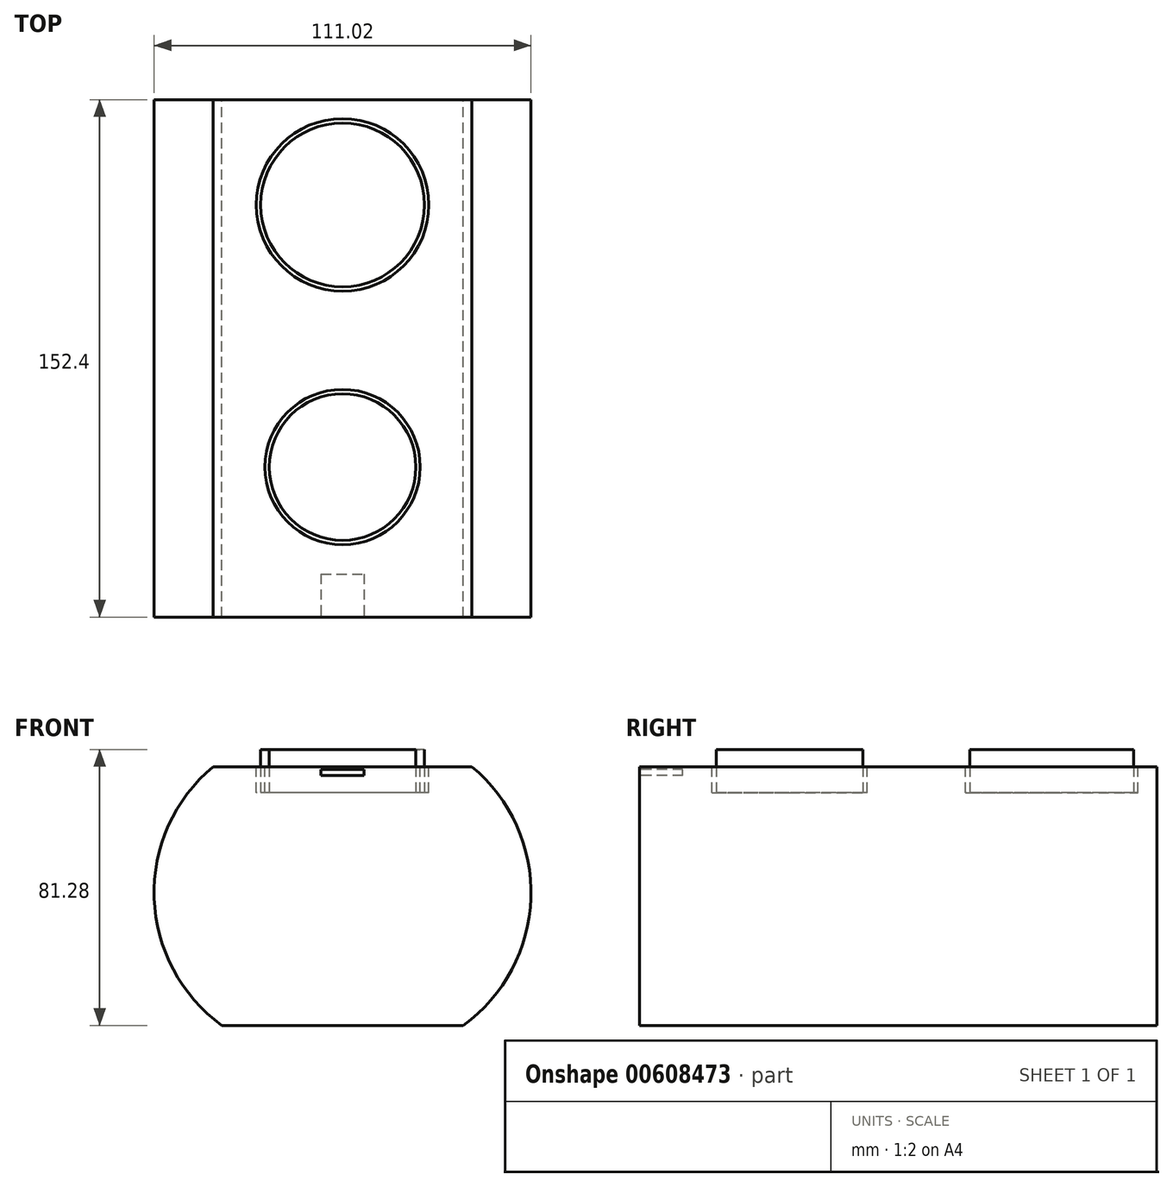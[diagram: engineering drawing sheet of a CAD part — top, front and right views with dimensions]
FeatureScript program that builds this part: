
annotation { "Feature Type Name" : "Feature", "Feature Type Description" : "" }
export const myFeature = defineFeature(function(context is Context, id is Id, definition is map)
    precondition{}
    {
        {
            var Q0;
            Q0=qCreatedBy(makeId("Front.planeOp"),FACE);
            var sketch = newSketch(context, id + "F0", { "sketchPlane" : qUnion([Q0])});
            skLineSegment(sketch, "E0", {"start": v(0, 0) * mm, "end": v(0, 76.2) * mm});
            skLineSegment(sketch, "E1", {"start": v(0, 76.2) * mm, "end": v(-38.1, 76.2) * mm});
            skLineSegment(sketch, "E2", {"start": v(0, 0) * mm, "end": v(-35.56, 0) * mm});
            skArc(sketch, "E3", {"start": v(-38.1, 76.2) * mm, "mid": v(-55.49, 37.48) * mm, "end": v(-35.56, 0) * mm});
            skLineSegment(sketch, "E4.MirrorCS", {"start": v(0, 0) * mm, "end": v(35.56, 0) * mm});
            skArc(sketch, "E5.MirrorCS", {"start": v(38.1, 76.2) * mm, "mid": v(55.49, 37.48) * mm, "end": v(35.56, 0) * mm});
            skLineSegment(sketch, "E6.MirrorCS", {"start": v(0, 76.2) * mm, "end": v(38.1, 76.2) * mm});
            skSolve(sketch);
        }
        {
            var Q0;
            Q0 = qSketchRegion(id + "F0", true);
            extrude(context, id + "F1", {"entities" : qUnion([Q0]), "depth" : 152.4 * mm, "offsetDistance" : 25.4 * mm});
        }
        {
            var Q0;
            Q0=makeQuery(id+"F1.opExtrude","SWEPT_FACE",FACE,{"disambiguationData":[OSD([sQuery(id+"F0.wireOp",EDGE,"E1"),sQuery(id+"F0.wireOp",EDGE,"E6.MirrorCS")])]});
            var sketch = newSketch(context, id + "F2", { "sketchPlane" : qUnion([Q0])});
            skCircle(sketch, "E7", {"center": v(0, -520.64) * mm, "radius": 35.86 * mm});
            skCircle(sketch, "E8", {"center": v(0, -297.7) * mm, "radius": 34.86 * mm});
            skSolve(sketch);
        }
        {
            var Q0;
            Q0 = qSketchRegion(id + "F2", true);
            extrude(context, id + "F3", {"entities" : qUnion([Q0]), "operationType" : NewBodyOperationType.REMOVE, "oppositeDirection" : true, "depth" : 7.62 * mm, "offsetDistance" : 25.4 * mm});
        }
        {
            var Q0;
            Q0=makeQuery(id+"F1.opExtrude","SWEPT_FACE",FACE,{"disambiguationData":[OSD([sQuery(id+"F0.wireOp",EDGE,"E1"),sQuery(id+"F0.wireOp",EDGE,"E6.MirrorCS")])]});
            var sketch = newSketch(context, id + "F4", { "sketchPlane" : qUnion([Q0])});
            skCircle(sketch, "E9", {"center": v(0, -31.02) * mm, "radius": 25.4 * mm});
            skSolve(sketch);
        }
        {
            var Q0;
            Q0=makeQuery(id+"F4.imprint","IMPRINT",FACE,{"disambiguationData":[TD([[makeQuery(id+"F4.imprint","IMPRINT",EDGE,{"derivedFrom":sQuery(id+"F4.wireOp",EDGE,"E9")}),1.0]])]});
            extrude(context, id + "F5", {"entities" : qUnion([Q0]), "operationType" : NewBodyOperationType.REMOVE, "oppositeDirection" : true, "depth" : 7.62 * mm, "offsetDistance" : 25.4 * mm});
        }
        {
            var Q0;
            Q0=makeQuery(id+"F5.boolean.opBoolean","COPY",FACE,{"derivedFrom":makeQuery(id+"F5.opExtrude","CAP_FACE",FACE,{"disambiguationData":[OSD([sQuery(id+"F4.wireOp",EDGE,"E9")])],"isStart":false})});
            var sketch = newSketch(context, id + "F6", { "sketchPlane" : qUnion([Q0])});
            skCircle(sketch, "E10", {"center": v(0, -31.02) * mm, "radius": 24.13 * mm});
            skSolve(sketch);
        }
        {
            var Q0;
            Q0=makeQuery(id+"F6.imprint","IMPRINT",FACE,{"disambiguationData":[TD([[makeQuery(id+"F6.imprint","IMPRINT",EDGE,{"derivedFrom":sQuery(id+"F6.wireOp",EDGE,"E10")}),1.0]])]});
            extrude(context, id + "F7", {"entities" : qUnion([Q0]), "operationType" : NewBodyOperationType.ADD, "depth" : 12.7 * mm, "offsetDistance" : 25.4 * mm});
        }
        {
            var Q0;
            Q0=makeQuery(id+"F1.opExtrude","SWEPT_FACE",FACE,{"disambiguationData":[OSD([sQuery(id+"F0.wireOp",EDGE,"E1"),sQuery(id+"F0.wireOp",EDGE,"E6.MirrorCS")])]});
            var sketch = newSketch(context, id + "F8", { "sketchPlane" : qUnion([Q0])});
            skCircle(sketch, "E11", {"center": v(0, -108.22) * mm, "radius": 22.86 * mm});
            skSolve(sketch);
        }
        {
            var Q0;
            Q0=makeQuery(id+"F8.imprint","IMPRINT",FACE,{"disambiguationData":[TD([[makeQuery(id+"F8.imprint","IMPRINT",EDGE,{"derivedFrom":sQuery(id+"F8.wireOp",EDGE,"E11")}),1.0]])]});
            extrude(context, id + "F9", {"entities" : qUnion([Q0]), "operationType" : NewBodyOperationType.REMOVE, "oppositeDirection" : true, "depth" : 7.62 * mm, "offsetDistance" : 25.4 * mm});
        }
        {
            var Q0;
            Q0=makeQuery(id+"F9.boolean.opBoolean","COPY",FACE,{"derivedFrom":makeQuery(id+"F9.opExtrude","CAP_FACE",FACE,{"disambiguationData":[OSD([sQuery(id+"F8.wireOp",EDGE,"E11")])],"isStart":false})});
            var sketch = newSketch(context, id + "F10", { "sketchPlane" : qUnion([Q0])});
            skCircle(sketch, "E12", {"center": v(0, -108.22) * mm, "radius": 21.59 * mm});
            skSolve(sketch);
        }
        {
            var Q0;
            Q0 = qSketchRegion(id + "F10", true);
            extrude(context, id + "F11", {"entities" : qUnion([Q0]), "operationType" : NewBodyOperationType.ADD, "depth" : 12.7 * mm, "offsetDistance" : 25.4 * mm});
        }
        {
            var Q0;
            Q0=makeQuery(id+"F1.opExtrude","CAP_FACE",FACE,{"disambiguationData":[OSD([sQuery(id+"F0.wireOp",EDGE,"E1"),sQuery(id+"F0.wireOp",EDGE,"E2"),sQuery(id+"F0.wireOp",EDGE,"E3"),sQuery(id+"F0.wireOp",EDGE,"E4.MirrorCS"),sQuery(id+"F0.wireOp",EDGE,"E5.MirrorCS"),sQuery(id+"F0.wireOp",EDGE,"E6.MirrorCS")])],"isStart":false});
            var sketch = newSketch(context, id + "F12", { "sketchPlane" : qUnion([Q0])});
            skLineSegment(sketch, "E13.bottom", {"start": v(-6.35, 73.66) * mm, "end": v(6.35, 73.66) * mm});
            skPoint(sketch, "E13.middle", {"position": v(0, 76.2) * mm});
            skLineSegment(sketch, "E14.top", {"start": v(-6.35, 75.38) * mm, "end": v(6.35, 75.38) * mm});
            skLineSegment(sketch, "E14.left", {"start": v(-6.35, 73.66) * mm, "end": v(-6.35, 75.38) * mm});
            skLineSegment(sketch, "E14.right", {"start": v(6.35, 73.66) * mm, "end": v(6.35, 75.38) * mm});
            skSolve(sketch);
        }
        {
            var Q0;
            Q0 = qSketchRegion(id + "F12", true);
            extrude(context, id + "F13", {"entities" : qUnion([Q0]), "operationType" : NewBodyOperationType.REMOVE, "oppositeDirection" : true, "depth" : 12.7 * mm, "offsetDistance" : 25.4 * mm});
        }
    });
